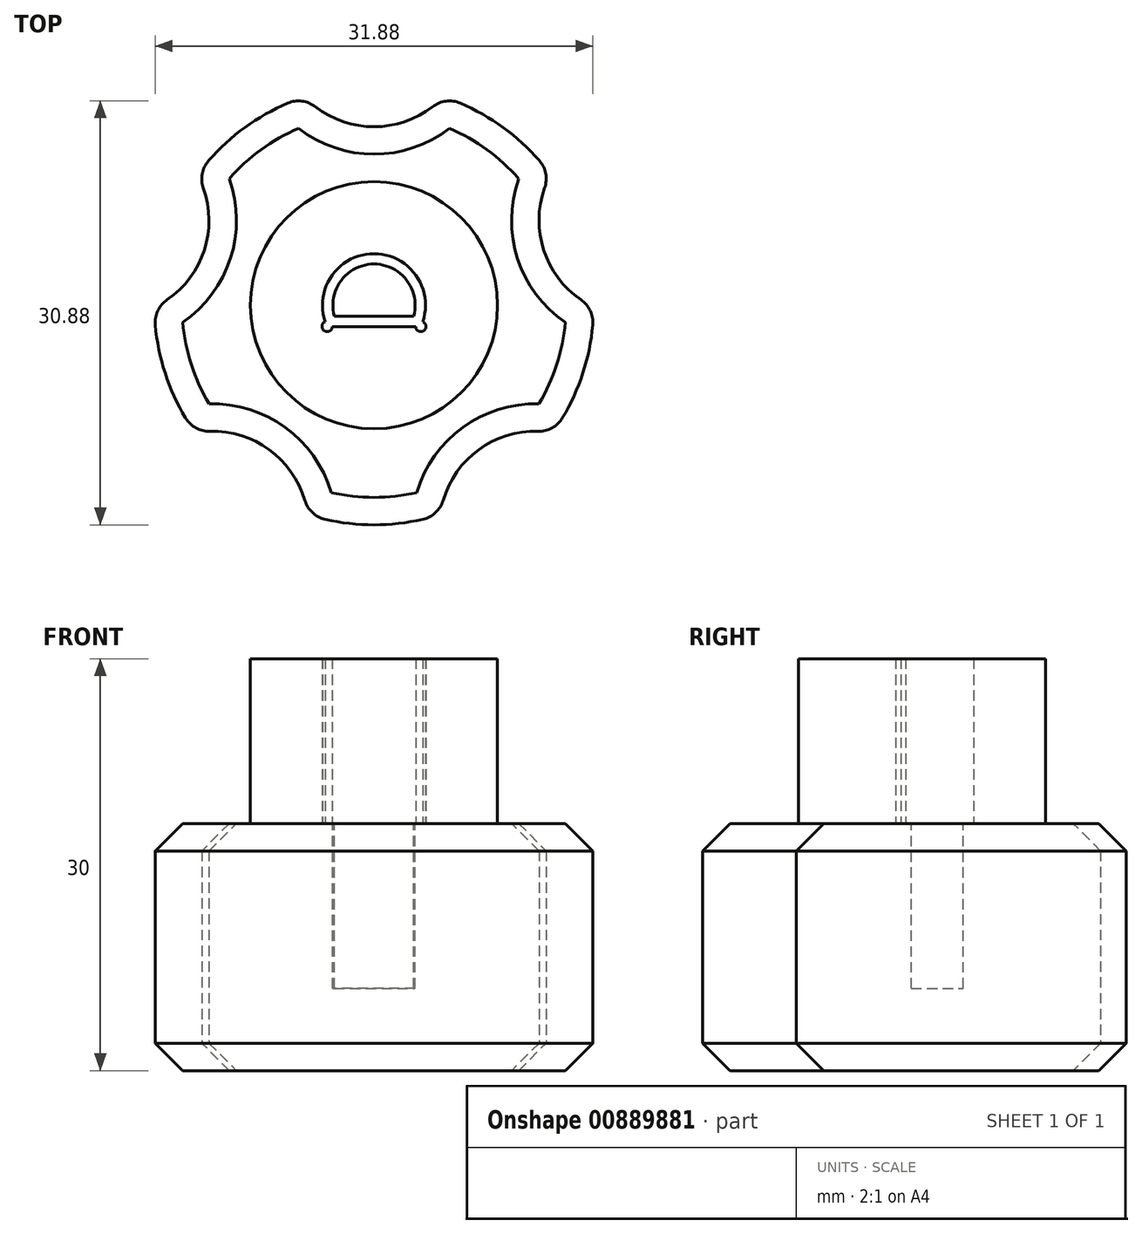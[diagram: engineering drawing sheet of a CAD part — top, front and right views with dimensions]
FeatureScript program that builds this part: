
annotation { "Feature Type Name" : "Feature", "Feature Type Description" : "" }
export const myFeature = defineFeature(function(context is Context, id is Id, definition is map)
    precondition{}
    {
        {
            assignVariable(context, id + "F0", {"name" : "KnobDiameter", "anyValue" : 32});
        }
        {
            var Q0;
            Q0=qCreatedBy(makeId("Top.planeOp"),FACE);
            var sketch = newSketch(context, id + "F1", { "sketchPlane" : qUnion([Q0])});
            skCircle(sketch, "E0", {"center": v(0, 0) * mm, "radius": 3.75 * mm});
            skLineSegment(sketch, "E1", {"start": v(-3.41, -1.55) * mm, "end": v(3.41, -1.55) * mm});
            skCircle(sketch, "E2", {"center": v(0, 0) * mm, "radius": 9 * mm});
            skArc(sketch, "E3", {"start": v(-6.28, 14.71) * mm, "mid": v(-9.4, 12.94) * mm, "end": v(-12.05, 10.52) * mm});
            skCircle(sketch, "E4", {"center": v(0, 0) * mm, "radius": 13 * mm, "construction": true});
            skArc(sketch, "E5", {"start": v(-4.28, 14.46) * mm, "mid": v(0, 13) * mm, "end": v(4.28, 14.46) * mm});
            skCircle(sketch, "E6", {"center": v(0, 0) * mm, "radius": 20 * mm, "construction": true});
            skArc(sketch, "E7.1.0", {"start": v(-15.07, 0.4) * mm, "mid": v(-12.36, 4.02) * mm, "end": v(-12.43, 8.54) * mm});
            skArc(sketch, "E7.2.0", {"start": v(-5.04, -14.21) * mm, "mid": v(-7.64, -10.52) * mm, "end": v(-11.96, -9.18) * mm});
            skArc(sketch, "E7.3.0", {"start": v(11.96, -9.18) * mm, "mid": v(7.64, -10.52) * mm, "end": v(5.04, -14.21) * mm});
            skArc(sketch, "E7.4.0", {"start": v(12.43, 8.54) * mm, "mid": v(12.36, 4.02) * mm, "end": v(15.07, 0.4) * mm});
            skCircle(sketch, "E8", {"center": v(-3.41, -1.55) * mm, "radius": 0.38 * mm});
            skCircle(sketch, "E9", {"center": v(3.41, -1.55) * mm, "radius": 0.38 * mm});
            skArc(sketch, "E10.trimOffspring", {"start": v(12.05, 10.52) * mm, "mid": v(9.4, 12.94) * mm, "end": v(6.28, 14.71) * mm});
            skArc(sketch, "E11.trimOffspring", {"start": v(13.73, -8.21) * mm, "mid": v(15.22, -4.94) * mm, "end": v(15.94, -1.43) * mm});
            skArc(sketch, "E12.trimOffspring", {"start": v(-3.56, -15.6) * mm, "mid": v(0, -16) * mm, "end": v(3.56, -15.6) * mm});
            skArc(sketch, "E13.trimOffspring", {"start": v(-15.94, -1.43) * mm, "mid": v(-15.22, -4.94) * mm, "end": v(-13.73, -8.21) * mm});
            skPoint(sketch, "E14.visualSharp", {"position": v(5.07, 15.18) * mm});
            skArc(sketch, "E14.filletArc", {"start": v(6.28, 14.71) * mm, "mid": v(5.25, 14.86) * mm, "end": v(4.28, 14.46) * mm});
            skPoint(sketch, "E15.visualSharp", {"position": v(12.87, 9.51) * mm});
            skArc(sketch, "E15.filletArc", {"start": v(12.43, 8.54) * mm, "mid": v(12.51, 9.58) * mm, "end": v(12.05, 10.52) * mm});
            skPoint(sketch, "E16.visualSharp", {"position": v(16, -0.13) * mm});
            skArc(sketch, "E16.filletArc", {"start": v(15.94, -1.43) * mm, "mid": v(15.75, -0.4) * mm, "end": v(15.07, 0.4) * mm});
            skPoint(sketch, "E17.visualSharp", {"position": v(13.02, -9.3) * mm});
            skArc(sketch, "E17.filletArc", {"start": v(11.96, -9.18) * mm, "mid": v(12.98, -8.94) * mm, "end": v(13.73, -8.21) * mm});
            skPoint(sketch, "E18.visualSharp", {"position": v(4.82, -15.26) * mm});
            skArc(sketch, "E18.filletArc", {"start": v(3.56, -15.6) * mm, "mid": v(4.5, -15.1) * mm, "end": v(5.04, -14.21) * mm});
            skPoint(sketch, "E19.visualSharp", {"position": v(-4.82, -15.26) * mm});
            skArc(sketch, "E19.filletArc", {"start": v(-5.04, -14.21) * mm, "mid": v(-4.5, -15.1) * mm, "end": v(-3.56, -15.6) * mm});
            skPoint(sketch, "E20.visualSharp", {"position": v(-13.02, -9.3) * mm});
            skArc(sketch, "E20.filletArc", {"start": v(-13.73, -8.21) * mm, "mid": v(-12.98, -8.94) * mm, "end": v(-11.96, -9.18) * mm});
            skPoint(sketch, "E21.visualSharp", {"position": v(-16, -0.13) * mm});
            skArc(sketch, "E21.filletArc", {"start": v(-15.07, 0.4) * mm, "mid": v(-15.75, -0.4) * mm, "end": v(-15.94, -1.43) * mm});
            skPoint(sketch, "E22.visualSharp", {"position": v(-12.87, 9.51) * mm});
            skArc(sketch, "E22.filletArc", {"start": v(-12.05, 10.52) * mm, "mid": v(-12.51, 9.58) * mm, "end": v(-12.43, 8.54) * mm});
            skPoint(sketch, "E23.visualSharp", {"position": v(-5.07, 15.18) * mm});
            skArc(sketch, "E23.filletArc", {"start": v(-4.28, 14.46) * mm, "mid": v(-5.25, 14.86) * mm, "end": v(-6.28, 14.71) * mm});
            skSolve(sketch);
        }
        {
            var Q0;
            Q0=makeQuery(id+"F1.imprint","IMPRINT",FACE,{"disambiguationData":[TD([[makeQuery(id+"F1.imprint","IMPRINT",EDGE,{"derivedFrom":sQuery(id+"F1.wireOp",EDGE,"E2")}),1.0]])]});
            var Q1;
            {var subQ0=sQuery(id+"F1.wireOp",EDGE,"E8");var subQ1=sQuery(id+"F1.wireOp",EDGE,"E0");var subQ2=makeQuery(id+"F1.imprint","INTERSECT",VERTEX,{"disambiguationData":[OD(1.0)],"derivedFrom":[subQ1,subQ0]});Q1=makeQuery(id+"F1.imprint","IMPRINT",FACE,{"disambiguationData":[TD([[makeQuery(id+"F1.imprint","IMPRINT",EDGE,{"disambiguationData":[TD([[subQ2,-1.0]])],"derivedFrom":subQ1}),1.0]])]});}
            extrude(context, id + "F2", {"entities" : qUnion([Q0, Q1]), "depth" : 12 * mm, "offsetDistance" : 25 * mm});
        }
        {
            var Q0;
            Q0=makeQuery(id+"F1.imprint","IMPRINT",FACE,{"disambiguationData":[TD([[makeQuery(id+"F1.imprint","IMPRINT",EDGE,{"derivedFrom":sQuery(id+"F1.wireOp",EDGE,"E2")}),-1.0]])]});
            var Q1;
            Q1=makeQuery(id+"F2.opExtrude","CAP_FACE",FACE,{"disambiguationData":[OSD([sQuery(id+"F1.wireOp",EDGE,"E0"),sQuery(id+"F1.wireOp",EDGE,"E1"),sQuery(id+"F1.wireOp",EDGE,"E2"),sQuery(id+"F1.wireOp",EDGE,"E8"),sQuery(id+"F1.wireOp",EDGE,"E9")])],"isStart":false});
            var Q2;
            {var subQ0=sQuery(id+"F1.wireOp",EDGE,"E8");var subQ1=sQuery(id+"F1.wireOp",EDGE,"E0");var subQ2=makeQuery(id+"F1.imprint","INTERSECT",VERTEX,{"disambiguationData":[OD(0.0)],"derivedFrom":[subQ1,subQ0]});Q2=makeQuery(id+"F1.imprint","IMPRINT",FACE,{"disambiguationData":[TD([[makeQuery(id+"F1.imprint","IMPRINT",EDGE,{"disambiguationData":[TD([[subQ2,1.0]])],"derivedFrom":subQ1}),1.0]])]});}
            var Q3;
            {var subQ0=sQuery(id+"F1.wireOp",EDGE,"E0");var subQ1=makeQuery(id+"F1.imprint","INTERSECT",VERTEX,{"disambiguationData":[OD(0.0)],"derivedFrom":[subQ0,sQuery(id+"F1.wireOp",EDGE,"E1")]});Q3=makeQuery(id+"F1.imprint","IMPRINT",FACE,{"disambiguationData":[TD([[makeQuery(id+"F1.imprint","IMPRINT",EDGE,{"disambiguationData":[TD([[subQ1,1.0]])],"derivedFrom":subQ0}),-1.0]])]});}
            var Q4;
            {var subQ0=sQuery(id+"F1.wireOp",EDGE,"E1");var subQ1=sQuery(id+"F1.wireOp",EDGE,"E0");var subQ2=makeQuery(id+"F1.imprint","INTERSECT",VERTEX,{"disambiguationData":[OD(0.0)],"derivedFrom":[subQ1,subQ0]});Q4=makeQuery(id+"F1.imprint","IMPRINT",FACE,{"disambiguationData":[TD([[makeQuery(id+"F1.imprint","IMPRINT",EDGE,{"disambiguationData":[TD([[subQ2,1.0]])],"derivedFrom":subQ1}),1.0]])]});}
            var Q5;
            {var subQ0=sQuery(id+"F1.wireOp",EDGE,"E1");var subQ1=sQuery(id+"F1.wireOp",EDGE,"E0");var subQ2=makeQuery(id+"F1.imprint","INTERSECT",VERTEX,{"disambiguationData":[OD(0.0)],"derivedFrom":[subQ1,subQ0]});Q5=makeQuery(id+"F1.imprint","IMPRINT",FACE,{"disambiguationData":[TD([[makeQuery(id+"F1.imprint","IMPRINT",EDGE,{"disambiguationData":[TD([[subQ2,-1.0]])],"derivedFrom":subQ1}),1.0]])]});}
            var Q6;
            {var subQ0=sQuery(id+"F1.wireOp",EDGE,"E1");var subQ1=sQuery(id+"F1.wireOp",EDGE,"E0");var subQ2=makeQuery(id+"F1.imprint","INTERSECT",VERTEX,{"disambiguationData":[OD(1.0)],"derivedFrom":[subQ1,subQ0]});Q6=makeQuery(id+"F1.imprint","IMPRINT",FACE,{"disambiguationData":[TD([[makeQuery(id+"F1.imprint","IMPRINT",EDGE,{"disambiguationData":[TD([[subQ2,-1.0]])],"derivedFrom":subQ1}),1.0]])]});}
            var Q7;
            {var subQ0=sQuery(id+"F1.wireOp",EDGE,"E1");var subQ1=sQuery(id+"F1.wireOp",EDGE,"E0");var subQ2=makeQuery(id+"F1.imprint","INTERSECT",VERTEX,{"disambiguationData":[OD(1.0)],"derivedFrom":[subQ1,subQ0]});Q7=makeQuery(id+"F1.imprint","IMPRINT",FACE,{"disambiguationData":[TD([[makeQuery(id+"F1.imprint","IMPRINT",EDGE,{"disambiguationData":[TD([[subQ2,1.0]])],"derivedFrom":subQ1}),1.0]])]});}
            var Q8;
            {var subQ0=sQuery(id+"F1.wireOp",EDGE,"E0");var subQ1=makeQuery(id+"F1.imprint","INTERSECT",VERTEX,{"disambiguationData":[OD(1.0)],"derivedFrom":[subQ0,sQuery(id+"F1.wireOp",EDGE,"E1")]});Q8=makeQuery(id+"F1.imprint","IMPRINT",FACE,{"disambiguationData":[TD([[makeQuery(id+"F1.imprint","IMPRINT",EDGE,{"disambiguationData":[TD([[subQ1,1.0]])],"derivedFrom":subQ0}),-1.0]])]});}
            extrude(context, id + "F3", {"entities" : qUnion([Q0, Q1, Q2, Q3, Q4, Q5, Q6, Q7, Q8]), "operationType" : NewBodyOperationType.ADD, "depth" : 18 * mm, "offsetDistance" : 25 * mm});
        }
        {
            var Q0;
            Q0=makeQuery(id+"F3.opExtrude","CAP_FACE",FACE,{"disambiguationData":[OSD([sQuery(id+"F1.wireOp",EDGE,"E0"),sQuery(id+"F1.wireOp",EDGE,"E1"),sQuery(id+"F1.wireOp",EDGE,"E8"),sQuery(id+"F1.wireOp",EDGE,"E9")])],"isStart":false});
            var sketch = newSketch(context, id + "F4", { "sketchPlane" : qUnion([Q0])});
            skCircle(sketch, "E24", {"center": v(0, 0) * mm, "radius": 3 * mm});
            skLineSegment(sketch, "E25", {"start": v(-2.9, -0.8) * mm, "end": v(2.9, -0.8) * mm});
            skSolve(sketch);
        }
        {
            var Q0;
            {var subQ0=sQuery(id+"F4.wireOp",EDGE,"E25");Q0=makeQuery(id+"F4.imprint","IMPRINT",FACE,{"disambiguationData":[TD([[makeQuery(id+"F4.imprint","IMPRINT",EDGE,{"derivedFrom":subQ0}),1.0]])]});}
            extrude(context, id + "F5", {"entities" : qUnion([Q0]), "operationType" : NewBodyOperationType.REMOVE, "oppositeDirection" : true, "depth" : 12 * mm, "offsetDistance" : 25 * mm});
        }
        {
            var Q0;
            Q0=makeQuery(id+"F3.opExtrude","CAP_EDGE",EDGE,{"disambiguationData":[OSD([sQuery(id+"F1.wireOp",EDGE,"E12.trimOffspring")])],"isStart":false});
            var Q1;
            Q1=makeQuery(id+"F3.opExtrude","CAP_EDGE",EDGE,{"disambiguationData":[OSD([sQuery(id+"F1.wireOp",EDGE,"E12.trimOffspring")])],"isStart":true});
            chamfer(context, id + "F6", {"entities" : qUnion([Q0, Q1]), "width" : (getVariable(context, 'KnobDiameter') / 16) * mm, "tangentPropagation" : true});
        }
    });
